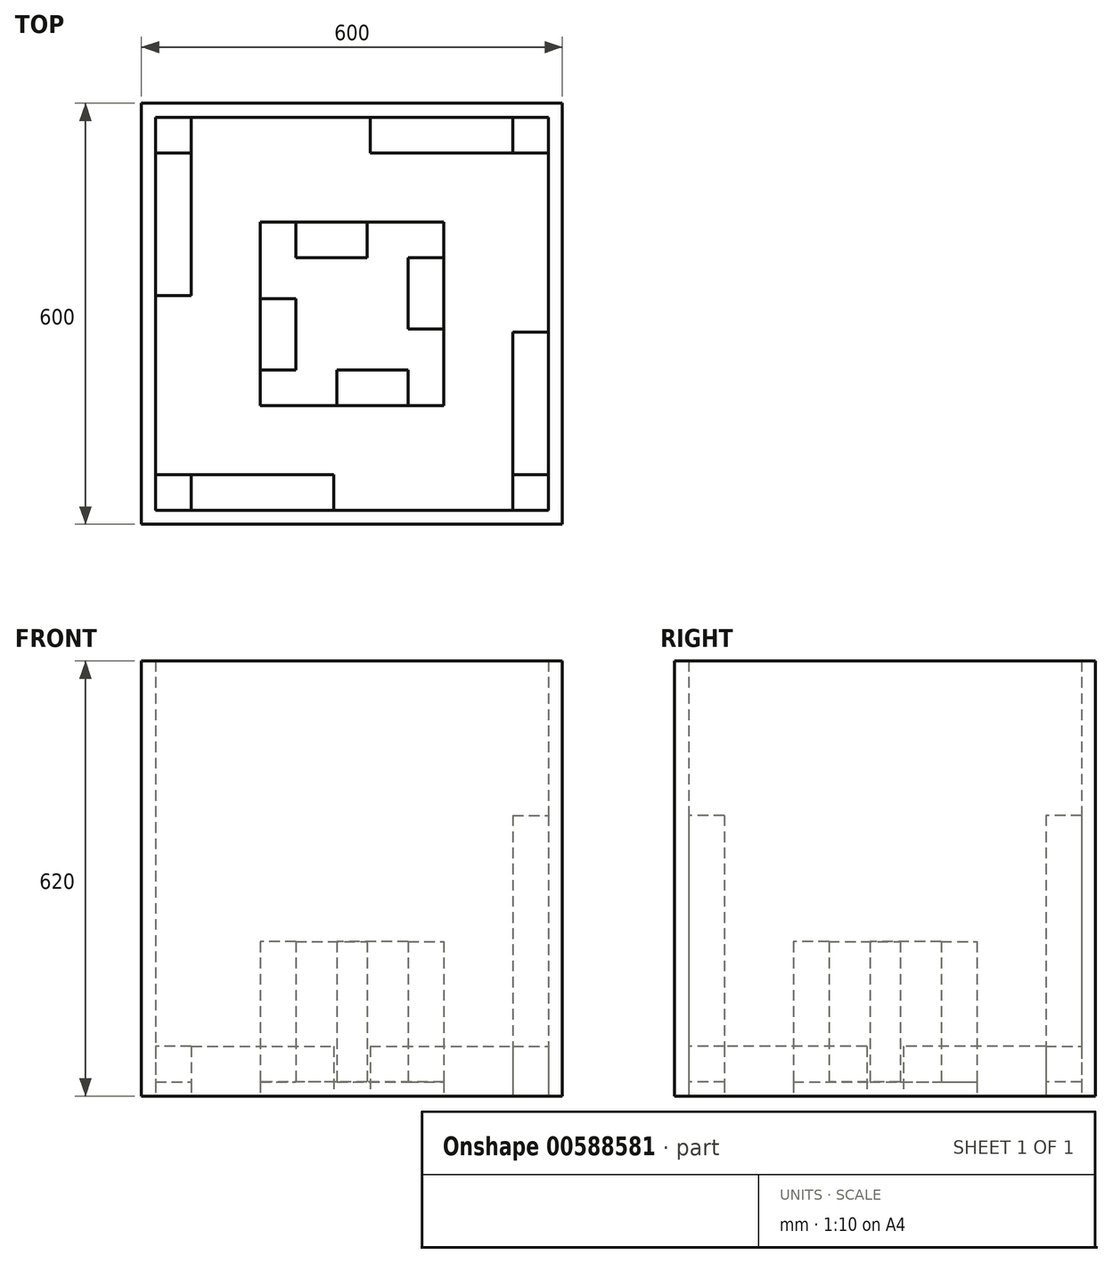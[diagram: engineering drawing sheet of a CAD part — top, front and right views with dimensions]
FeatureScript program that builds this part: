
annotation { "Feature Type Name" : "Feature", "Feature Type Description" : "" }
export const myFeature = defineFeature(function(context is Context, id is Id, definition is map)
    precondition{}
    {
        {
            var Q0;
            Q0=qCreatedBy(makeId("Top.planeOp"),FACE);
            var sketch = newSketch(context, id + "F0", { "sketchPlane" : qUnion([Q0])});
            skLineSegment(sketch, "E0.bottom", {"start": v(300, 300) * mm, "end": v(-300, 300) * mm});
            skLineSegment(sketch, "E0.top", {"start": v(300, -300) * mm, "end": v(-300, -300) * mm});
            skLineSegment(sketch, "E0.left", {"start": v(300, 300) * mm, "end": v(300, -300) * mm});
            skLineSegment(sketch, "E0.right", {"start": v(-300, 300) * mm, "end": v(-300, -300) * mm});
            skLineSegment(sketch, "E1.bottom", {"start": v(-280, 280) * mm, "end": v(280, 280) * mm});
            skLineSegment(sketch, "E1.top", {"start": v(-280, -280) * mm, "end": v(280, -280) * mm});
            skLineSegment(sketch, "E1.left", {"start": v(-280, 280) * mm, "end": v(-280, -280) * mm});
            skLineSegment(sketch, "E1.right", {"start": v(280, 280) * mm, "end": v(280, -280) * mm});
            skLineSegment(sketch, "E2", {"start": v(-80, 80) * mm, "end": v(-80, 130.8) * mm});
            skLineSegment(sketch, "E3", {"start": v(-80, 130.8) * mm, "end": v(21.6, 130.8) * mm});
            skLineSegment(sketch, "E4", {"start": v(21.6, 130.8) * mm, "end": v(21.6, 80) * mm});
            skLineSegment(sketch, "E5", {"start": v(21.6, 80) * mm, "end": v(-80, 80) * mm});
            skLineSegment(sketch, "E6", {"start": v(80, 80) * mm, "end": v(130.8, 80) * mm});
            skLineSegment(sketch, "E7", {"start": v(130.8, 80) * mm, "end": v(130.8, -21.6) * mm});
            skLineSegment(sketch, "E8", {"start": v(80, -80) * mm, "end": v(80, -130.8) * mm});
            skLineSegment(sketch, "E9", {"start": v(80, -130.8) * mm, "end": v(-21.6, -130.8) * mm});
            skLineSegment(sketch, "E10", {"start": v(-80, -80) * mm, "end": v(-130.8, -80) * mm});
            skLineSegment(sketch, "E11", {"start": v(-130.8, -80) * mm, "end": v(-130.8, 21.6) * mm});
            skLineSegment(sketch, "E12", {"start": v(-130.8, 21.6) * mm, "end": v(-80, 21.6) * mm});
            skLineSegment(sketch, "E13", {"start": v(-80, 21.6) * mm, "end": v(-80, -80) * mm});
            skLineSegment(sketch, "E14", {"start": v(-21.6, -130.8) * mm, "end": v(-21.6, -80) * mm});
            skLineSegment(sketch, "E15", {"start": v(-21.6, -80) * mm, "end": v(80, -80) * mm});
            skLineSegment(sketch, "E16", {"start": v(130.8, -21.6) * mm, "end": v(80, -21.6) * mm});
            skLineSegment(sketch, "E17", {"start": v(80, -21.6) * mm, "end": v(80, 80) * mm});
            skLineSegment(sketch, "E18", {"start": v(-280, 280) * mm, "end": v(-229.2, 280) * mm});
            skLineSegment(sketch, "E19", {"start": v(-229.2, 280) * mm, "end": v(-229.2, 229.2) * mm});
            skLineSegment(sketch, "E20", {"start": v(-229.2, 229.2) * mm, "end": v(-280, 229.2) * mm});
            skLineSegment(sketch, "E21", {"start": v(-280, 229.2) * mm, "end": v(-280, 280) * mm});
            skLineSegment(sketch, "E22", {"start": v(-229.2, 229.2) * mm, "end": v(-229.2, 26) * mm});
            skLineSegment(sketch, "E23", {"start": v(-229.2, 26) * mm, "end": v(-280, 26) * mm});
            skLineSegment(sketch, "E24", {"start": v(-280, 26) * mm, "end": v(-280, 229.2) * mm});
            skLineSegment(sketch, "E25", {"start": v(-280, -280) * mm, "end": v(-280, -229.2) * mm});
            skLineSegment(sketch, "E26", {"start": v(-280, -229.2) * mm, "end": v(-229.2, -229.2) * mm});
            skLineSegment(sketch, "E27", {"start": v(-229.2, -229.2) * mm, "end": v(-229.2, -280) * mm});
            skLineSegment(sketch, "E28", {"start": v(-229.2, -280) * mm, "end": v(-280, -280) * mm});
            skLineSegment(sketch, "E29", {"start": v(-229.2, -229.2) * mm, "end": v(-26, -229.2) * mm});
            skLineSegment(sketch, "E30", {"start": v(-26, -229.2) * mm, "end": v(-26, -280) * mm});
            skLineSegment(sketch, "E31", {"start": v(229.2, -280) * mm, "end": v(229.2, -229.2) * mm});
            skLineSegment(sketch, "E32", {"start": v(229.2, -229.2) * mm, "end": v(280, -229.2) * mm});
            skLineSegment(sketch, "E33", {"start": v(280, -229.2) * mm, "end": v(280, -280) * mm});
            skLineSegment(sketch, "E34", {"start": v(229.2, -229.2) * mm, "end": v(229.2, -26) * mm});
            skLineSegment(sketch, "E35", {"start": v(229.2, -26) * mm, "end": v(280, -26) * mm});
            skLineSegment(sketch, "E36", {"start": v(280, -26) * mm, "end": v(280, -229.2) * mm});
            skLineSegment(sketch, "E37", {"start": v(229.2, 280) * mm, "end": v(229.2, 229.2) * mm});
            skLineSegment(sketch, "E38", {"start": v(229.2, 229.2) * mm, "end": v(280, 229.2) * mm});
            skLineSegment(sketch, "E39", {"start": v(229.2, 229.2) * mm, "end": v(26, 229.2) * mm});
            skLineSegment(sketch, "E40", {"start": v(26, 229.2) * mm, "end": v(26, 280) * mm});
            skLineSegment(sketch, "E41.top", {"start": v(-130.8, 130.8) * mm, "end": v(-80, 130.8) * mm});
            skLineSegment(sketch, "E41.left", {"start": v(-130.8, 21.6) * mm, "end": v(-130.8, 130.8) * mm});
            skLineSegment(sketch, "E42.bottom", {"start": v(80, -130.8) * mm, "end": v(130.8, -130.8) * mm});
            skLineSegment(sketch, "E42.top", {"start": v(80, -21.6) * mm, "end": v(130.8, -21.6) * mm});
            skLineSegment(sketch, "E42.right", {"start": v(130.8, -130.8) * mm, "end": v(130.8, -21.6) * mm});
            skLineSegment(sketch, "E43.bottom", {"start": v(130.8, -130.8) * mm, "end": v(-130.8, -130.8) * mm});
            skLineSegment(sketch, "E43.top", {"start": v(130.8, 130.8) * mm, "end": v(-130.8, 130.8) * mm});
            skLineSegment(sketch, "E43.left", {"start": v(130.8, -130.8) * mm, "end": v(130.8, 130.8) * mm});
            skLineSegment(sketch, "E43.right", {"start": v(-130.8, -130.8) * mm, "end": v(-130.8, 130.8) * mm});
            skSolve(sketch);
        }
        {
            var Q0;
            Q0=makeQuery(id+"F0.imprint","IMPRINT",FACE,{"disambiguationData":[TD([[makeQuery(id+"F0.imprint","IMPRINT",EDGE,{"derivedFrom":sQuery(id+"F0.wireOp",EDGE,"E1.left")}),1.0]])]});
            var Q1;
            {var subQ3=sQuery(id+"F0.wireOp",EDGE,"E2");Q1=makeQuery(id+"F0.imprint","IMPRINT",FACE,{"disambiguationData":[TD([[makeQuery(id+"F0.imprint","IMPRINT",EDGE,{"derivedFrom":subQ3}),1.0]])]});}
            extrude(context, id + "F1", {"entities" : qUnion([Q0, Q1]), "depth" : 20 * mm, "offsetDistance" : 25 * mm});
        }
        {
            var Q0;
            Q0=makeQuery(id+"F0.imprint","IMPRINT",FACE,{"disambiguationData":[TD([[makeQuery(id+"F0.imprint","IMPRINT",EDGE,{"derivedFrom":sQuery(id+"F0.wireOp",EDGE,"E0.bottom")}),1.0]])]});
            extrude(context, id + "F2", {"entities" : qUnion([Q0]), "operationType" : NewBodyOperationType.ADD, "depth" : 620 * mm, "offsetDistance" : 25 * mm});
        }
        {
            var Q0;
            Q0=makeQuery(id+"F0.imprint","IMPRINT",FACE,{"disambiguationData":[TD([[makeQuery(id+"F0.imprint","IMPRINT",EDGE,{"derivedFrom":sQuery(id+"F0.wireOp",EDGE,"E10")}),-1.0]])]});
            var Q1;
            Q1=makeQuery(id+"F0.imprint","IMPRINT",FACE,{"disambiguationData":[TD([[makeQuery(id+"F0.imprint","IMPRINT",EDGE,{"derivedFrom":sQuery(id+"F0.wireOp",EDGE,"E2")}),-1.0]])]});
            var Q2;
            Q2=makeQuery(id+"F0.imprint","IMPRINT",FACE,{"disambiguationData":[TD([[makeQuery(id+"F0.imprint","IMPRINT",EDGE,{"derivedFrom":sQuery(id+"F0.wireOp",EDGE,"E6")}),-1.0]])]});
            var Q3;
            Q3=makeQuery(id+"F0.imprint","IMPRINT",FACE,{"disambiguationData":[TD([[makeQuery(id+"F0.imprint","IMPRINT",EDGE,{"derivedFrom":sQuery(id+"F0.wireOp",EDGE,"E8")}),-1.0]])]});
            extrude(context, id + "F3", {"entities" : qUnion([Q0, Q1, Q2, Q3]), "operationType" : NewBodyOperationType.ADD, "depth" : 220 * mm, "offsetDistance" : 25 * mm});
        }
        {
            var Q0;
            Q0=makeQuery(id+"F0.imprint","IMPRINT",FACE,{"disambiguationData":[TD([[makeQuery(id+"F0.imprint","IMPRINT",EDGE,{"derivedFrom":sQuery(id+"F0.wireOp",EDGE,"E20")}),1.0]])]});
            var Q1;
            Q1=makeQuery(id+"F0.imprint","IMPRINT",FACE,{"disambiguationData":[TD([[makeQuery(id+"F0.imprint","IMPRINT",EDGE,{"derivedFrom":sQuery(id+"F0.wireOp",EDGE,"E32")}),1.0]])]});
            var Q2;
            {var subQ0=sQuery(id+"F0.wireOp",EDGE,"E27");Q2=makeQuery(id+"F0.imprint","IMPRINT",FACE,{"disambiguationData":[TD([[makeQuery(id+"F0.imprint","IMPRINT",EDGE,{"derivedFrom":subQ0}),1.0]])]});}
            var Q3;
            {var subQ0=sQuery(id+"F0.wireOp",EDGE,"E37");Q3=makeQuery(id+"F0.imprint","IMPRINT",FACE,{"disambiguationData":[TD([[makeQuery(id+"F0.imprint","IMPRINT",EDGE,{"derivedFrom":subQ0}),-1.0]])]});}
            extrude(context, id + "F4", {"entities" : qUnion([Q0, Q1, Q2, Q3]), "operationType" : NewBodyOperationType.ADD, "depth" : 70.8 * mm, "offsetDistance" : 25 * mm});
        }
        {
            var Q0;
            Q0=makeQuery(id+"F0.imprint","IMPRINT",FACE,{"disambiguationData":[TD([[makeQuery(id+"F0.imprint","IMPRINT",EDGE,{"derivedFrom":sQuery(id+"F0.wireOp",EDGE,"E18")}),-1.0]])]});
            var Q1;
            Q1=makeQuery(id+"F0.imprint","IMPRINT",FACE,{"disambiguationData":[TD([[makeQuery(id+"F0.imprint","IMPRINT",EDGE,{"derivedFrom":sQuery(id+"F0.wireOp",EDGE,"E25")}),-1.0]])]});
            var Q2;
            {var subQ2=sQuery(id+"F0.wireOp",EDGE,"E31");Q2=makeQuery(id+"F0.imprint","IMPRINT",FACE,{"disambiguationData":[TD([[makeQuery(id+"F0.imprint","IMPRINT",EDGE,{"derivedFrom":subQ2}),-1.0]])]});}
            var Q3;
            {var subQ3=sQuery(id+"F0.wireOp",EDGE,"E37");Q3=makeQuery(id+"F0.imprint","IMPRINT",FACE,{"disambiguationData":[TD([[makeQuery(id+"F0.imprint","IMPRINT",EDGE,{"derivedFrom":subQ3}),1.0]])]});}
            extrude(context, id + "F5", {"entities" : qUnion([Q0, Q1, Q2, Q3]), "operationType" : NewBodyOperationType.ADD, "depth" : 400 * mm, "offsetDistance" : 25 * mm});
        }
    });
